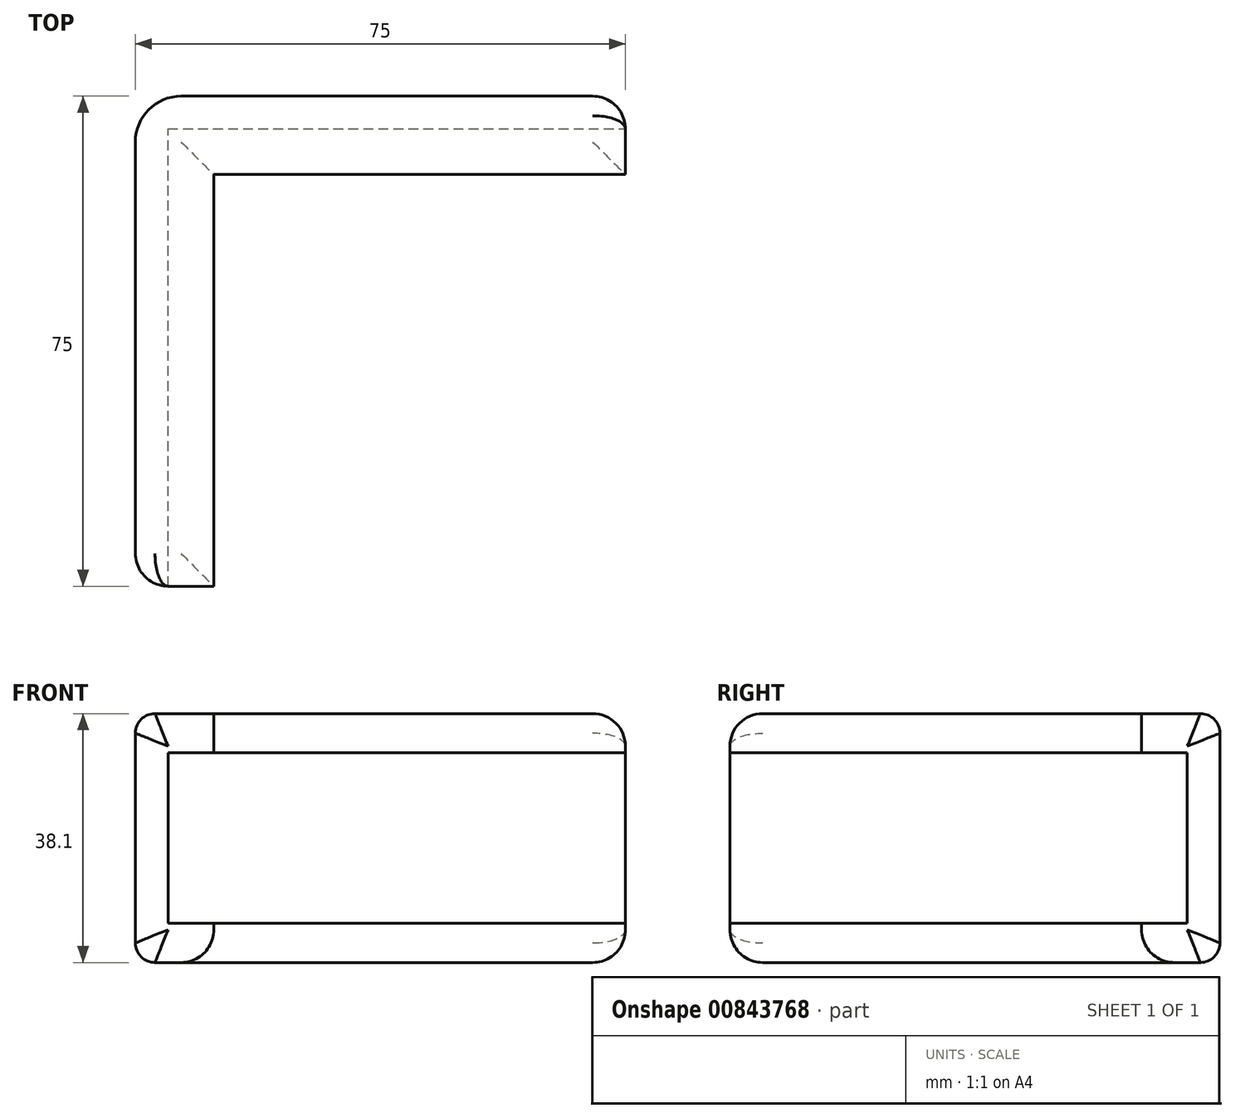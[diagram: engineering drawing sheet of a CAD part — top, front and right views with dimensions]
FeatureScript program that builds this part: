
annotation { "Feature Type Name" : "Feature", "Feature Type Description" : "" }
export const myFeature = defineFeature(function(context is Context, id is Id, definition is map)
    precondition{}
    {
        {
            var Q0;
            Q0=qCreatedBy(makeId("Front.planeOp"),FACE);
            var sketch = newSketch(context, id + "F0", { "sketchPlane" : qUnion([Q0])});
            skLineSegment(sketch, "E0.bottom", {"start": v(-37.5, 19.05) * mm, "end": v(37.5, 19.05) * mm});
            skLineSegment(sketch, "E0.top", {"start": v(-37.5, -19.05) * mm, "end": v(37.5, -19.05) * mm});
            skLineSegment(sketch, "E0.left", {"start": v(-37.5, 19.05) * mm, "end": v(-37.5, -19.05) * mm});
            skLineSegment(sketch, "E0.right", {"start": v(37.5, 19.05) * mm, "end": v(37.5, -19.05) * mm});
            skPoint(sketch, "E1", {"position": v(0, 0) * mm});
            skPoint(sketch, "E1.positionSnap0", {"position": v(0, -19.05) * mm});
            skPoint(sketch, "E1.positionSnap1", {"position": v(37.5, 0) * mm});
            skSolve(sketch);
        }
        {
            var Q0;
            Q0=makeQuery(id+"F0.imprint","IMPRINT",FACE,{"disambiguationData":[TD([[makeQuery(id+"F0.imprint","IMPRINT",EDGE,{"derivedFrom":sQuery(id+"F0.wireOp",EDGE,"E0.bottom")}),-1.0]])]});
            var Q1;
            Q1 = qSketchRegion(id + "F0", true);
            extrude(context, id + "F1", {"entities" : qUnion([Q0, Q1]), "depth" : 75 * mm, "offsetDistance" : 25 * mm});
        }
        {
            var Q0;
            Q0=makeQuery(id+"F1.opExtrude","CAP_EDGE",EDGE,{"disambiguationData":[OSD([sQuery(id+"F0.wireOp",EDGE,"E0.top")])],"isStart":true});
            var Q1;
            Q1=makeQuery(id+"F1.opExtrude","SWEPT_EDGE",EDGE,{"disambiguationData":[OSD([sQuery(id+"F0.wireOp",EDGE,"E0.top"),sQuery(id+"F0.wireOp",EDGE,"E0.left")])]});
            var Q2;
            Q2=makeQuery(id+"F1.opExtrude","CAP_EDGE",EDGE,{"disambiguationData":[OSD([sQuery(id+"F0.wireOp",EDGE,"E0.bottom")])],"isStart":true});
            var Q3;
            Q3=makeQuery(id+"F1.opExtrude","SWEPT_EDGE",EDGE,{"disambiguationData":[OSD([sQuery(id+"F0.wireOp",EDGE,"E0.bottom"),sQuery(id+"F0.wireOp",EDGE,"E0.left")])]});
            fillet(context, id + "F2", {"entities" : qUnion([Q0, Q1, Q2, Q3]), "radius" : 3 * mm, "tangentPropagation" : true, "allowEdgeOverflow" : false});
        }
        {
            var Q0;
            Q0=makeQuery(id+"F1.opExtrude","CAP_EDGE",EDGE,{"disambiguationData":[OSD([sQuery(id+"F0.wireOp",EDGE,"E0.left")])],"isStart":true});
            fillet(context, id + "F3", {"entities" : qUnion([Q0]), "radius" : 7 * mm, "tangentPropagation" : true, "allowEdgeOverflow" : false});
        }
        {
            var Q0;
            Q0=makeQuery(id+"F1.opExtrude","SWEPT_FACE",FACE,{"disambiguationData":[OSD([sQuery(id+"F0.wireOp",EDGE,"E0.bottom")])]});
            var sketch = newSketch(context, id + "F4", { "sketchPlane" : qUnion([Q0])});
            skLineSegment(sketch, "E2.bottom", {"start": v(37.5, -12) * mm, "end": v(-25.5, -12) * mm});
            skLineSegment(sketch, "E2.top", {"start": v(37.5, -75) * mm, "end": v(-25.5, -75) * mm});
            skLineSegment(sketch, "E2.left", {"start": v(37.5, -12) * mm, "end": v(37.5, -75) * mm});
            skLineSegment(sketch, "E2.right", {"start": v(-25.5, -12) * mm, "end": v(-25.5, -75) * mm});
            skSolve(sketch);
        }
        {
            var Q0;
            Q0 = qSketchRegion(id + "F4", true);
            extrude(context, id + "F5", {"entities" : qUnion([Q0]), "operationType" : NewBodyOperationType.REMOVE, "endBound" : BoundingType.THROUGH_ALL, "oppositeDirection" : true, "depth" : 25 * mm, "offsetDistance" : 25 * mm});
        }
        {
            var Q0;
            Q0=makeQuery(id+"F5.boolean.opBoolean","COPY",FACE,{"derivedFrom":makeQuery(id+"F5.opExtrude","SWEPT_FACE",FACE,{"disambiguationData":[OSD([sQuery(id+"F4.wireOp",EDGE,"E2.right")])]})});
            var sketch = newSketch(context, id + "F6", { "sketchPlane" : qUnion([Q0])});
            skLineSegment(sketch, "E3.bottom", {"start": v(-75, 13.05) * mm, "end": v(-5, 13.05) * mm});
            skLineSegment(sketch, "E3.top", {"start": v(-75, -13.05) * mm, "end": v(-5, -13.05) * mm});
            skLineSegment(sketch, "E3.left", {"start": v(-75, 13.05) * mm, "end": v(-75, -13.05) * mm});
            skLineSegment(sketch, "E3.right", {"start": v(-5, 13.05) * mm, "end": v(-5, -13.05) * mm});
            skLineSegment(sketch, "E4", {"start": v(-75, 0) * mm, "end": v(-12, 0) * mm, "construction": true});
            skPoint(sketch, "E4.endSnap0", {"position": v(-75, 0) * mm});
            skSolve(sketch);
        }
        {
            var Q0;
            Q0 = qSketchRegion(id + "F6", true);
            extrude(context, id + "F7", {"entities" : qUnion([Q0]), "operationType" : NewBodyOperationType.REMOVE, "oppositeDirection" : true, "depth" : 7 * mm, "offsetDistance" : 25 * mm});
        }
        {
            var Q0;
            Q0=makeQuery(id+"F5.boolean.opBoolean","COPY",FACE,{"derivedFrom":makeQuery(id+"F5.opExtrude","SWEPT_FACE",FACE,{"disambiguationData":[OSD([sQuery(id+"F4.wireOp",EDGE,"E2.bottom")])]})});
            var sketch = newSketch(context, id + "F8", { "sketchPlane" : qUnion([Q0])});
            skLineSegment(sketch, "E5.bottom", {"start": v(-25.5, 13.05) * mm, "end": v(37.5, 13.05) * mm});
            skLineSegment(sketch, "E5.top", {"start": v(-25.5, -13.05) * mm, "end": v(37.5, -13.05) * mm});
            skLineSegment(sketch, "E5.left", {"start": v(-25.5, 13.05) * mm, "end": v(-25.5, -13.05) * mm});
            skLineSegment(sketch, "E5.right", {"start": v(37.5, 13.05) * mm, "end": v(37.5, -13.05) * mm});
            skSolve(sketch);
        }
        {
            var Q0;
            Q0 = qSketchRegion(id + "F8", true);
            extrude(context, id + "F9", {"entities" : qUnion([Q0]), "operationType" : NewBodyOperationType.REMOVE, "oppositeDirection" : true, "depth" : 7 * mm, "offsetDistance" : 25 * mm});
        }
        {
            var Q0;
            Q0=makeQuery(id+"F1.opExtrude","CAP_EDGE",EDGE,{"disambiguationData":[OSD([sQuery(id+"F0.wireOp",EDGE,"E0.top")])],"isStart":false});
            var Q1;
            {var subQ0=sQuery(id+"F0.wireOp",EDGE,"E0.left");var subQ1=sQuery(id+"F0.wireOp",EDGE,"E0.top");Q1=makeQuery(id+"F2.opFillet","BLEND_EDGE",EDGE,{"blendedFrom":[makeQuery(id+"F1.opExtrude","SWEPT_EDGE",EDGE,{"disambiguationData":[OSD([subQ1,subQ0])]}),makeQuery(id+"F1.opExtrude","CAP_FACE",FACE,{"disambiguationData":[OSD([sQuery(id+"F0.wireOp",EDGE,"E0.bottom"),subQ1,subQ0,sQuery(id+"F0.wireOp",EDGE,"E0.right")])],"isStart":false})],"blendedInto":[makeQuery(id+"F1.opExtrude","CAP_FACE",FACE,{"disambiguationData":[OSD([sQuery(id+"F0.wireOp",EDGE,"E0.bottom"),subQ1,subQ0,sQuery(id+"F0.wireOp",EDGE,"E0.right")])],"isStart":false})]});}
            var Q2;
            Q2=makeQuery(id+"F1.opExtrude","CAP_EDGE",EDGE,{"disambiguationData":[OSD([sQuery(id+"F0.wireOp",EDGE,"E0.left")])],"isStart":false});
            var Q3;
            {var subQ0=sQuery(id+"F0.wireOp",EDGE,"E0.left");var subQ1=sQuery(id+"F0.wireOp",EDGE,"E0.bottom");Q3=makeQuery(id+"F2.opFillet","BLEND_EDGE",EDGE,{"blendedFrom":[makeQuery(id+"F1.opExtrude","SWEPT_EDGE",EDGE,{"disambiguationData":[OSD([subQ1,subQ0])]}),makeQuery(id+"F1.opExtrude","CAP_FACE",FACE,{"disambiguationData":[OSD([subQ1,sQuery(id+"F0.wireOp",EDGE,"E0.top"),subQ0,sQuery(id+"F0.wireOp",EDGE,"E0.right")])],"isStart":false})],"blendedInto":[makeQuery(id+"F1.opExtrude","CAP_FACE",FACE,{"disambiguationData":[OSD([subQ1,sQuery(id+"F0.wireOp",EDGE,"E0.top"),subQ0,sQuery(id+"F0.wireOp",EDGE,"E0.right")])],"isStart":false})]});}
            var Q4;
            Q4=makeQuery(id+"F1.opExtrude","CAP_EDGE",EDGE,{"disambiguationData":[OSD([sQuery(id+"F0.wireOp",EDGE,"E0.bottom")])],"isStart":false});
            var Q5;
            Q5=makeQuery(id+"F1.opExtrude","SWEPT_EDGE",EDGE,{"disambiguationData":[OSD([sQuery(id+"F0.wireOp",EDGE,"E0.bottom"),sQuery(id+"F0.wireOp",EDGE,"E0.right")])]});
            var Q6;
            Q6=makeQuery(id+"F2.opFillet","BLEND_EDGE",EDGE,{"blendedFrom":[makeQuery(id+"F1.opExtrude","CAP_EDGE",EDGE,{"disambiguationData":[OSD([sQuery(id+"F0.wireOp",EDGE,"E0.bottom")])],"isStart":true}),makeQuery(id+"F1.opExtrude","SWEPT_FACE",FACE,{"disambiguationData":[OSD([sQuery(id+"F0.wireOp",EDGE,"E0.right")])]})],"blendedInto":[makeQuery(id+"F1.opExtrude","SWEPT_FACE",FACE,{"disambiguationData":[OSD([sQuery(id+"F0.wireOp",EDGE,"E0.right")])]})]});
            var Q7;
            Q7=makeQuery(id+"F1.opExtrude","CAP_EDGE",EDGE,{"disambiguationData":[OSD([sQuery(id+"F0.wireOp",EDGE,"E0.right")])],"isStart":true});
            var Q8;
            Q8=makeQuery(id+"F2.opFillet","BLEND_EDGE",EDGE,{"blendedFrom":[makeQuery(id+"F1.opExtrude","CAP_EDGE",EDGE,{"disambiguationData":[OSD([sQuery(id+"F0.wireOp",EDGE,"E0.top")])],"isStart":true}),makeQuery(id+"F1.opExtrude","SWEPT_FACE",FACE,{"disambiguationData":[OSD([sQuery(id+"F0.wireOp",EDGE,"E0.right")])]})],"blendedInto":[makeQuery(id+"F1.opExtrude","SWEPT_FACE",FACE,{"disambiguationData":[OSD([sQuery(id+"F0.wireOp",EDGE,"E0.right")])]})]});
            var Q9;
            Q9=makeQuery(id+"F1.opExtrude","SWEPT_EDGE",EDGE,{"disambiguationData":[OSD([sQuery(id+"F0.wireOp",EDGE,"E0.top"),sQuery(id+"F0.wireOp",EDGE,"E0.right")])]});
            var Q10;
            Q10=makeQuery(id+"F5.boolean.opBoolean","COPY",EDGE,{"derivedFrom":makeQuery(id+"F5.opExtrude","CAP_EDGE",EDGE,{"disambiguationData":[OSD([sQuery(id+"F4.wireOp",EDGE,"E2.right")])],"isStart":true})});
            var Q11;
            Q11=makeQuery(id+"F5.boolean.opBoolean","COPY",EDGE,{"derivedFrom":makeQuery(id+"F5.opExtrude","CAP_EDGE",EDGE,{"disambiguationData":[OSD([sQuery(id+"F4.wireOp",EDGE,"E2.bottom")])],"isStart":true})});
            var Q12;
            Q12=makeQuery(id+"F5.boolean.opBoolean","INTERSECT",EDGE,{"derivedFrom":[makeQuery(id+"F1.opExtrude","SWEPT_FACE",FACE,{"disambiguationData":[OSD([sQuery(id+"F0.wireOp",EDGE,"E0.top")])]}),makeQuery(id+"F5.opExtrude","SWEPT_FACE",FACE,{"disambiguationData":[OSD([sQuery(id+"F4.wireOp",EDGE,"E2.right")])]})]});
            var Q13;
            Q13=makeQuery(id+"F5.boolean.opBoolean","INTERSECT",EDGE,{"derivedFrom":[makeQuery(id+"F1.opExtrude","SWEPT_FACE",FACE,{"disambiguationData":[OSD([sQuery(id+"F0.wireOp",EDGE,"E0.top")])]}),makeQuery(id+"F5.opExtrude","SWEPT_FACE",FACE,{"disambiguationData":[OSD([sQuery(id+"F4.wireOp",EDGE,"E2.bottom")])]})]});
            var Q14;
            {var subQ0=sQuery(id+"F0.wireOp",EDGE,"E0.bottom");var subQ1=sQuery(id+"F4.wireOp",EDGE,"E2.right");Q14=makeQuery(id+"F7.boolean.opBoolean","SPLIT",EDGE,{"disambiguationData":[TD([makeQuery(id+"F1.opExtrude","SWEPT_FACE",FACE,{"disambiguationData":[OSD([subQ0])]})])],"derivedFrom":makeQuery(id+"F5.boolean.opBoolean","COPY",EDGE,{"derivedFrom":makeQuery(id+"F5.opExtrude","SWEPT_EDGE",EDGE,{"disambiguationData":[OSD([subQ0,sQuery(id+"F4.wireOp",EDGE,"E2.top"),subQ1])]})})});}
            var Q15;
            {var subQ0=sQuery(id+"F0.wireOp",EDGE,"E0.top");var subQ1=sQuery(id+"F0.wireOp",EDGE,"E0.bottom");var subQ2=sQuery(id+"F4.wireOp",EDGE,"E2.right");Q15=makeQuery(id+"F7.boolean.opBoolean","SPLIT",EDGE,{"disambiguationData":[TD([makeQuery(id+"F1.opExtrude","SWEPT_FACE",FACE,{"disambiguationData":[OSD([subQ0])]})])],"derivedFrom":makeQuery(id+"F5.boolean.opBoolean","COPY",EDGE,{"derivedFrom":makeQuery(id+"F5.opExtrude","SWEPT_EDGE",EDGE,{"disambiguationData":[OSD([subQ1,sQuery(id+"F4.wireOp",EDGE,"E2.top"),subQ2])]})})});}
            var Q16;
            {var subQ0=sQuery(id+"F4.wireOp",EDGE,"E2.bottom");var subQ1=sQuery(id+"F0.wireOp",EDGE,"E0.right");Q16=makeQuery(id+"F9.boolean.opBoolean","SPLIT",EDGE,{"disambiguationData":[TD([makeQuery(id+"F1.opExtrude","SWEPT_FACE",FACE,{"disambiguationData":[OSD([sQuery(id+"F0.wireOp",EDGE,"E0.top")])]})])],"derivedFrom":makeQuery(id+"F5.boolean.opBoolean","COPY",EDGE,{"derivedFrom":makeQuery(id+"F5.opExtrude","SWEPT_EDGE",EDGE,{"disambiguationData":[OSD([sQuery(id+"F0.wireOp",EDGE,"E0.bottom"),subQ1,subQ0,sQuery(id+"F4.wireOp",EDGE,"E2.left")])]})})});}
            var Q17;
            {var subQ0=sQuery(id+"F4.wireOp",EDGE,"E2.bottom");var subQ1=sQuery(id+"F0.wireOp",EDGE,"E0.right");var subQ2=sQuery(id+"F0.wireOp",EDGE,"E0.bottom");Q17=makeQuery(id+"F9.boolean.opBoolean","SPLIT",EDGE,{"disambiguationData":[TD([makeQuery(id+"F1.opExtrude","SWEPT_FACE",FACE,{"disambiguationData":[OSD([subQ2])]})])],"derivedFrom":makeQuery(id+"F5.boolean.opBoolean","COPY",EDGE,{"derivedFrom":makeQuery(id+"F5.opExtrude","SWEPT_EDGE",EDGE,{"disambiguationData":[OSD([subQ2,subQ1,subQ0,sQuery(id+"F4.wireOp",EDGE,"E2.left")])]})})});}
            fillet(context, id + "F10", {"entities" : qUnion([Q0, Q1, Q2, Q3, Q4, Q5, Q6, Q7, Q8, Q9, Q10, Q11, Q12, Q13, Q14, Q15, Q16, Q17]), "radius" : 5 * mm, "tangentPropagation" : true, "allowEdgeOverflow" : false});
        }
    });
